# Revit family: 19 Zoll Switch MS400990M
name_source: partatom
category: Datengeräte
units: mm (PartAtom-declared; Revit-internal decimal feet)

## family parameters
Arbeitsebenenbasiert = Nein
Beim Laden mit Abzugskörper schneiden = Nein
Bemaßung runder Anschluss = Durchmesser verwenden
Beschriftungsausrichtung beibehalten = Nein
Gemeinsam genutzt = Nein
Immer vertikal = Ja
OmniClass-Nummer = 23.85.50.17
OmniClass-Titel = Communication and Data Processing Equipment
Raumberechnungspunkt = Nein
Teiletyp = Normal

## types (1)
- 19 Zoll Switch MS400990M
    Anschluss 1 = 4x 1/10GBase-X SFP+-Slots
    Anschluss 2 = 24x 100/1000Base-X SFP-Slots
    Anschluss 3 = 8x Combo
    Anschluss 4 = Konsolenport (RJ-45)
    Artikelnummer = MS400990M
    Ausführung = managed Switch
    Beschreibung = 28-Port 10G Multi Fiber L2/L3 Switch 19"
    Hersteller = MICROSENS
    Spannung Input = int. 100~240VAC (C14)
    Vorgabe-Ansicht = 0 mm  [stored 0 ft]

note: [stored X ft] marks values corroborated as IEEE doubles in the binary element streams (Revit-internal decimal feet)
